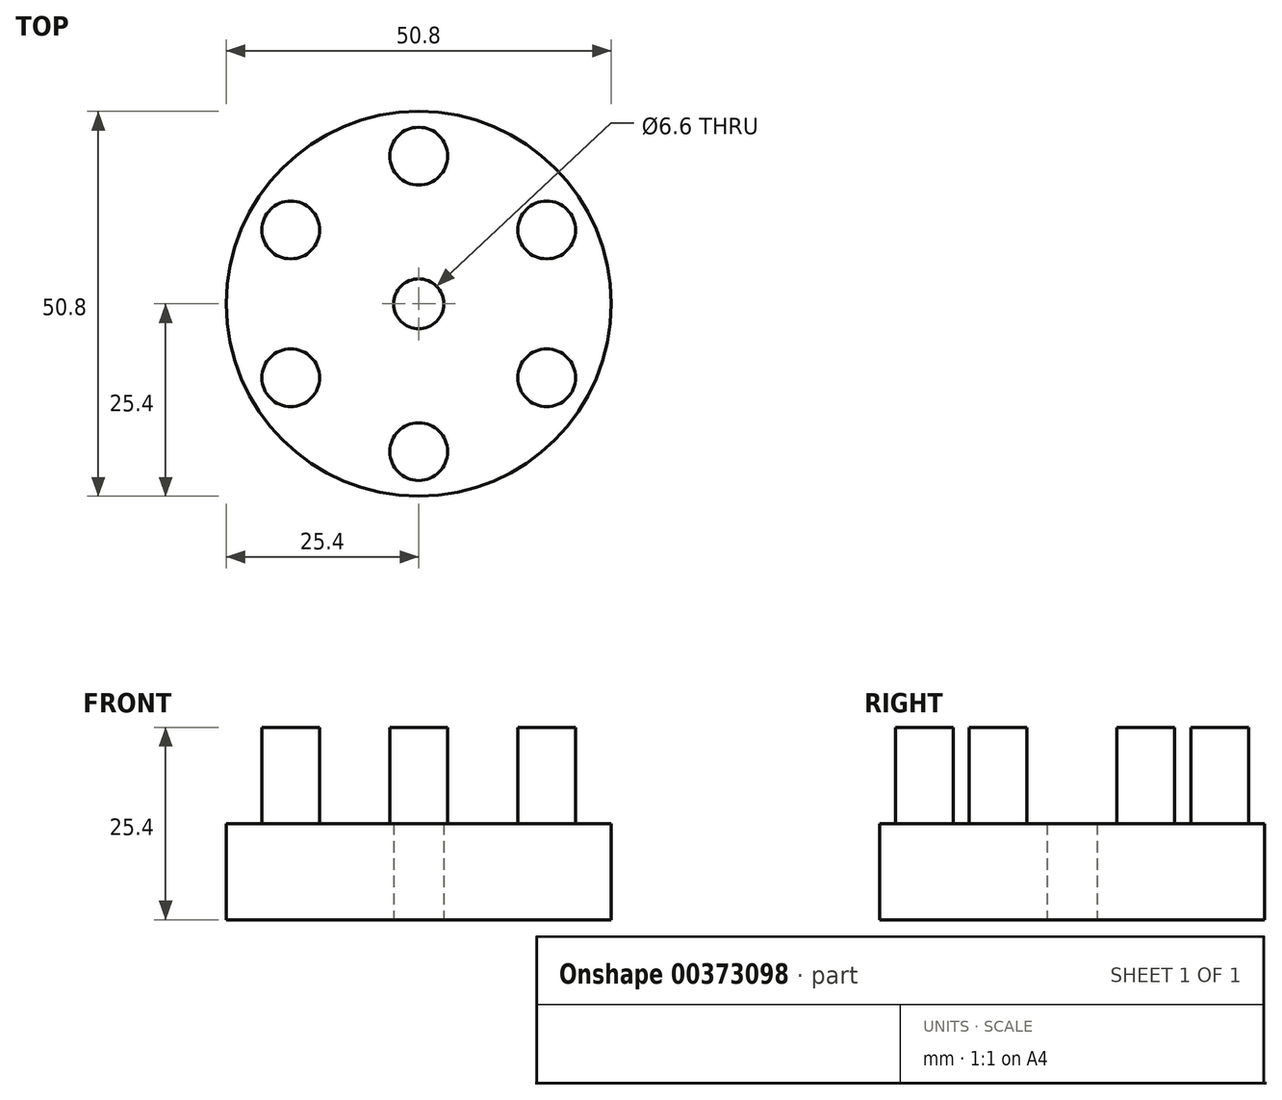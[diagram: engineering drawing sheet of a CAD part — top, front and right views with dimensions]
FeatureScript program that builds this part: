
annotation { "Feature Type Name" : "Feature", "Feature Type Description" : "" }
export const myFeature = defineFeature(function(context is Context, id is Id, definition is map)
    precondition{}
    {
        {
            var Q0;
            Q0=qCreatedBy(makeId("Top.planeOp"),FACE);
            var sketch = newSketch(context, id + "F0", { "sketchPlane" : qUnion([Q0])});
            skCircle(sketch, "E0", {"center": v(0, 0) * mm, "radius": 25.4 * mm});
            skSolve(sketch);
        }
        {
            var Q0;
            Q0=qCreatedBy(makeId("Top.planeOp"),FACE);
            var sketch = newSketch(context, id + "F1", { "sketchPlane" : qUnion([Q0])});
            skCircle(sketch, "E1", {"center": v(0, 19.5) * mm, "radius": 3.81 * mm});
            skCircle(sketch, "E2.1.0", {"center": v(-16.9, 9.75) * mm, "radius": 3.81 * mm});
            skCircle(sketch, "E2.2.0", {"center": v(-16.9, -9.75) * mm, "radius": 3.81 * mm});
            skCircle(sketch, "E2.3.0", {"center": v(0, -19.5) * mm, "radius": 3.81 * mm});
            skCircle(sketch, "E2.4.0", {"center": v(16.9, -9.75) * mm, "radius": 3.81 * mm});
            skCircle(sketch, "E2.5.0", {"center": v(16.9, 9.75) * mm, "radius": 3.81 * mm});
            skPoint(sketch, "E2.center", {"position": v(0, 0) * mm});
            skSolve(sketch);
        }
        {
            var Q0;
            Q0 = qSketchRegion(id + "F0", true);
            extrude(context, id + "F2", {"entities" : qUnion([Q0]), "depth" : 12.7 * mm});
        }
        {
            var Q0;
            Q0 = qSketchRegion(id + "F1", true);
            extrude(context, id + "F3", {"entities" : qUnion([Q0]), "operationType" : NewBodyOperationType.ADD, "depth" : 25.4 * mm});
        }
        {
            var Q0;
            Q0=qCreatedBy(makeId("Top.planeOp"),FACE);
            var sketch = newSketch(context, id + "F4", { "sketchPlane" : qUnion([Q0])});
            skCircle(sketch, "E3", {"center": v(0, 0) * mm, "radius": 3.3 * mm});
            skSolve(sketch);
        }
        {
            var Q0;
            Q0 = qSketchRegion(id + "F4", true);
            extrude(context, id + "F5", {"entities" : qUnion([Q0]), "operationType" : NewBodyOperationType.REMOVE, "depth" : 25.4 * mm});
        }
    });
